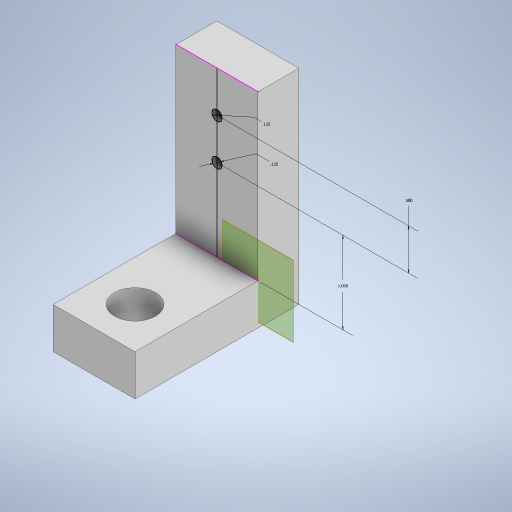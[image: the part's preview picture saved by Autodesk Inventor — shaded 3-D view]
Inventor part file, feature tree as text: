
AUTODESK INVENTOR PART (.ipt)
format: ipt  version: 2023 (Build 270158000, 158)  size: 256,512 bytes
history: native  units: in
note: dims shown in document units (in); Inventor stores cm internally (conversion verified against a paired STEP export)
features: sketch x3, plane x2, extrude x2
ambient origin geometry x8: Origin, YZ Plane, XZ Plane, XY Plane, X Axis, Y Axis, Z Axis, Center Point
bodies: Body1 (feature_tree)
feature tree (7):
  sketch  "Sketch1"  dims[d0=0.5in d1=1.0in]
  plane  "Work Plane1"
  sketch  "Sketch3"  dims[d2=1.5in d3=0.5in]
  plane  "Work Plane2"
  extrude  "Extrusion7"  Depth=1.0in
  extrude  "Extrusion8"  Depth=0.5in
  sketch  "Sketch4"  dims[d4=0.5in d23=0.125in d24=0.125in d25=1.0in d26=0.5in d29=0.5in d30=0.125in d31=0.125in d32=1.0in d36=0.5in d37=0.5in d38=0.0in d39=0.5in d40=0.0in]
